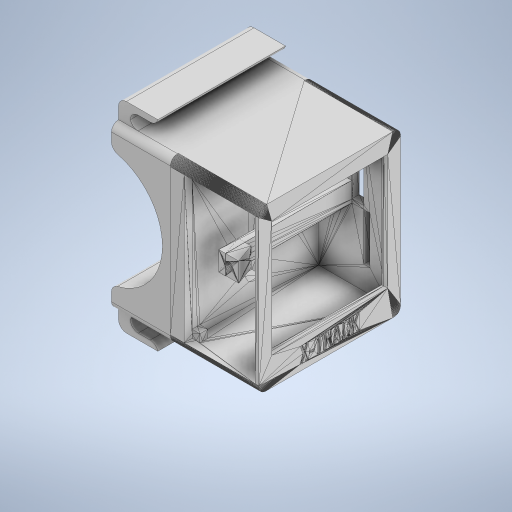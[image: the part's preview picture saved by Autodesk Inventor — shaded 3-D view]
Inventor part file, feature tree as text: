
AUTODESK INVENTOR PART (.ipt)
format: ipt  version: 2023 (Build 270158000, 158)  size: 1,662,464 bytes
history: native  units: in
note: dims shown in document units (in); Inventor stores cm internally (conversion verified against a paired STEP export)
features: fillet x10, sketch x7, extrude x6, imported_body x1
ambient origin geometry x8: Origin, YZ Plane, XZ Plane, XY Plane, X Axis, Y Axis, Z Axis, Center Point
bodies: Solid1 (feature_tree)
feature tree (24):
  sketch  "Sketch1"  dims[d0=0.0709in d1=0.0709in]
  extrude  "Extrusion1"  Depth=0.0709in
  extrude  "Extrusion2"  Depth=0.0709in
  fillet  "Fillet1"  Radius=0.5906in
  fillet  "Fillet2"  Radius=1.1811in
  extrude  "Extrusion3"  Depth=0.0787in
  extrude  "Extrusion4"  Depth=0.3937in
  extrude  "Extrusion5"  Depth=0.3937in
  extrude  "Extrusion6"  Depth=0.0787in
  fillet  "Fillet3"  [1 undecoded]
  fillet  "Fillet4"  Radius=0.2756in
  fillet  "Fillet5"  Radius=0.1378in
  fillet  "Fillet6"  [1 undecoded]
  fillet  "Fillet7"  Radius=0.0787in
  fillet  "Fillet8"  Radius=0.0787in
  fillet  "Fillet9"  Radius=0.0787in
  fillet  "Fillet10"  Radius=0.0787in
  sketch  "Sketch2"  dims[d2=0.0709in d3=0.0709in d4=0.5906in d5=0.0in d6=1.1811in]
  sketch  "Sketch4"  dims[d7=1.4719in d8=0.0in d9=0.0787in]
  sketch  "Sketch6"  dims[d10=0.0787in d11=0.3937in]
  sketch  "Sketch7"  dims[d12=0.1969in d13=0.0in d14=0.3937in]
  sketch  "Sketch8"  dims[d15=0.1969in d16=0.0in d17=0.2756in d18=0.0in d19=0.0in d20=0.2756in d21=0.1378in d22=0.0in d23=0.0in d24=0.0787in d25=0.0787in d26=0.0787in d27=0.0787in]
  sketch  "Sketch9"  dims[d28=0.0787in d29=0.0787in d30=0.0787in d31=0.0787in]
  imported_body  "Base1"
note: 2 required parameter values undecoded (feature->parameter linkage not recoverable at this tier; creation-order binding heuristic only, values carry confidence <= 0.55)
